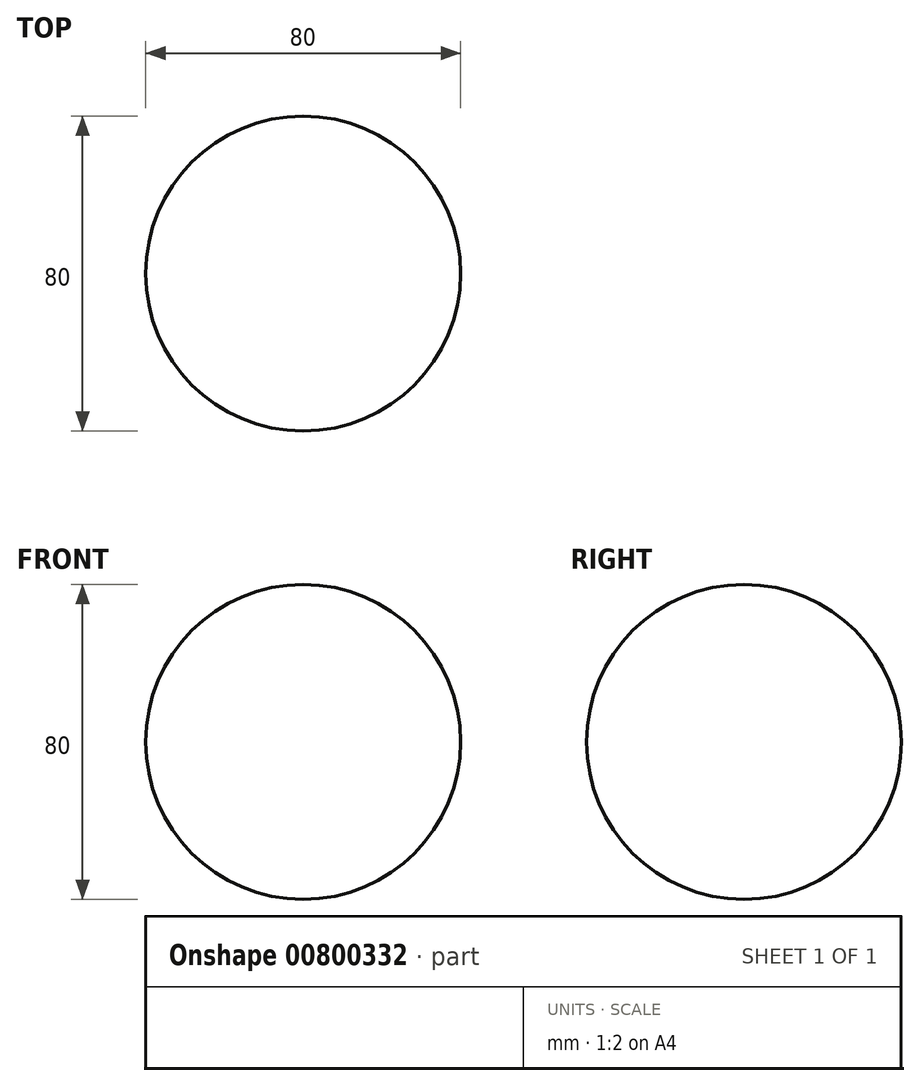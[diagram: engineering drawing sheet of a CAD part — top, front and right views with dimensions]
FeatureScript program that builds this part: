
annotation { "Feature Type Name" : "Feature", "Feature Type Description" : "" }
export const myFeature = defineFeature(function(context is Context, id is Id, definition is map)
    precondition{}
    {
        {
            var Q0;
            Q0=qCreatedBy(makeId("Front.planeOp"),FACE);
            var sketch = newSketch(context, id + "F0", { "sketchPlane" : qUnion([Q0])});
            skArc(sketch, "E0", {"start": v(40, 0) * mm, "mid": v(0, 40) * mm, "end": v(-40, 0) * mm});
            skLineSegment(sketch, "E1", {"start": v(-40, 0) * mm, "end": v(40, 0) * mm});
            skSolve(sketch);
        }
        {
            var Q0;
            Q0 = qSketchRegion(id + "F0", true);
            var Q1;
            Q1=sQuery(id+"F0.wireOp",EDGE,"E1");
            revolve(context, id + "F1", {"surfaceOperationType" : NewSurfaceOperationType.NEW, "entities" : qUnion([Q0]), "axis" : qUnion([Q1]), "revolveType" : RevolveType.FULL});
        }
        {
            var Q0;
            Q0=qCreatedBy(makeId("Front.planeOp"),FACE);
            var sketch = newSketch(context, id + "F2", { "sketchPlane" : qUnion([Q0])});
            skArc(sketch, "E2", {"start": v(37.96, 13.91) * mm, "mid": v(44.64, 37.57) * mm, "end": v(32.94, 59.2) * mm});
            skSolve(sketch);
        }
        {
            var Q0;
            Q0=sQuery(id+"F2.wireOp",VERTEX,"E2.end");
            var Q1;
            Q1=qCreatedBy(makeId("Right.planeOp"),FACE);
            cPlane(context, id + "F3", {"entities" : qUnion([Q0, Q1]), "cplaneType" : CPlaneType.PLANE_POINT, "offset" : 25 * mm, "width" : 150 * mm, "height" : 150 * mm});
        }
    });
